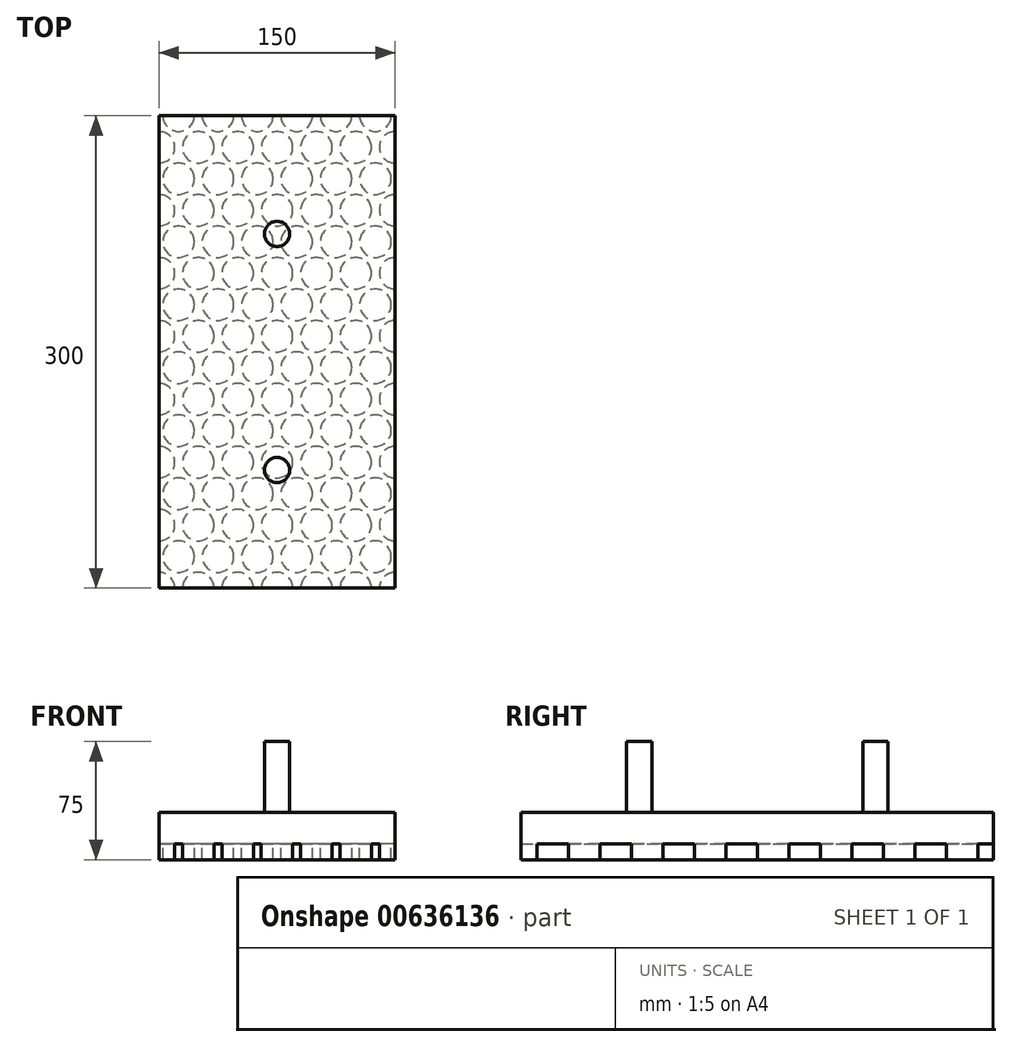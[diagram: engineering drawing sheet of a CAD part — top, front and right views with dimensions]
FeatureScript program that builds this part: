
annotation { "Feature Type Name" : "Feature", "Feature Type Description" : "" }
export const myFeature = defineFeature(function(context is Context, id is Id, definition is map)
    precondition{}
    {
        {
            var Q0;
            Q0=qCreatedBy(makeId("Top.planeOp"),FACE);
            var sketch = newSketch(context, id + "F0", { "sketchPlane" : qUnion([Q0])});
            skLineSegment(sketch, "E0.bottom", {"start": v(75, 150) * mm, "end": v(-75, 150) * mm});
            skLineSegment(sketch, "E0.top", {"start": v(75, -150) * mm, "end": v(-75, -150) * mm});
            skLineSegment(sketch, "E0.left", {"start": v(75, 150) * mm, "end": v(75, -150) * mm});
            skLineSegment(sketch, "E0.right", {"start": v(-75, 150) * mm, "end": v(-75, -150) * mm});
            skPoint(sketch, "E0.middle", {"position": v(0, 0) * mm});
            skSolve(sketch);
        }
        {
            var Q0;
            Q0=qSketchRegion(id+"F0",true);
            extrude(context, id + "F1", {"entities" : qUnion([Q0]), "oppositeDirection" : true, "depth" : 20 * mm, "offsetDistance" : 25 * mm});
        }
        {
            var Q0;
            Q0=makeQuery(id+"F1.opExtrude","CAP_FACE",FACE,{"disambiguationData":[OSD([sQuery(id+"F0.wireOp",EDGE,"E0.bottom"),sQuery(id+"F0.wireOp",EDGE,"E0.top"),sQuery(id+"F0.wireOp",EDGE,"E0.left"),sQuery(id+"F0.wireOp",EDGE,"E0.right"),sQuery(id+"F0.wireOp",EDGE,"dzeue0mq-ryTN-MEcJ-6Cr2-TIuR5wwS6aSh"),sQuery(id+"F0.wireOp",EDGE,"DPBKmNIL-XfQO-MkqB-CjDe-bxSWGcwg6vfk"),sQuery(id+"F0.wireOp",EDGE,"v2nlQ9jK-8eDu-H6yK-LcaL-di8VHofIcNa3"),sQuery(id+"F0.wireOp",EDGE,"Z1CVN7Bm-QXrQ-2ffn-gUqZ-VcZKbfZv5ewL")])],"isStart":true});
            var sketch = newSketch(context, id + "F2", { "sketchPlane" : qUnion([Q0])});
            skCircle(sketch, "E1", {"center": v(0, 75) * mm, "radius": 8 * mm});
            skCircle(sketch, "E2", {"center": v(0, -75) * mm, "radius": 8 * mm});
            skSolve(sketch);
        }
        {
            var Q0;
            Q0=qSketchRegion(id+"F2",true);
            extrude(context, id + "F3", {"entities" : qUnion([Q0]), "operationType" : NewBodyOperationType.ADD, "depth" : 45 * mm, "offsetDistance" : 25 * mm});
        }
        {
            var Q0;
            Q0=makeQuery(id+"F1.opExtrude","CAP_FACE",FACE,{"disambiguationData":[OSD([sQuery(id+"F0.wireOp",EDGE,"E0.bottom"),sQuery(id+"F0.wireOp",EDGE,"E0.top"),sQuery(id+"F0.wireOp",EDGE,"E0.left"),sQuery(id+"F0.wireOp",EDGE,"E0.right")])],"isStart":false});
            var sketch = newSketch(context, id + "F4", { "sketchPlane" : qUnion([Q0])});
            skCircle(sketch, "E3", {"center": v(-75.01, 150) * mm, "radius": 10 * mm});
            skCircle(sketch, "E4", {"center": v(-62.5, 130) * mm, "radius": 10 * mm});
            skCircle(sketch, "E5.0.1.0", {"center": v(-75, 110) * mm, "radius": 10 * mm});
            skCircle(sketch, "E5.0.2.0", {"center": v(-75, 70) * mm, "radius": 10 * mm});
            skCircle(sketch, "E5.0.3.0", {"center": v(-75, 30) * mm, "radius": 10 * mm});
            skCircle(sketch, "E5.0.4.0", {"center": v(-75, -10) * mm, "radius": 10 * mm});
            skCircle(sketch, "E5.0.5.0", {"center": v(-75, -50) * mm, "radius": 10 * mm});
            skCircle(sketch, "E5.0.6.0", {"center": v(-75, -90) * mm, "radius": 10 * mm});
            skCircle(sketch, "E5.0.7.0", {"center": v(-75, -130) * mm, "radius": 10 * mm});
            skCircle(sketch, "E5.1.0.0", {"center": v(-50.01, 150) * mm, "radius": 10 * mm});
            skCircle(sketch, "E5.1.1.0", {"center": v(-50, 110) * mm, "radius": 10 * mm});
            skCircle(sketch, "E5.1.2.0", {"center": v(-50, 70) * mm, "radius": 10 * mm});
            skCircle(sketch, "E5.1.3.0", {"center": v(-50, 30) * mm, "radius": 10 * mm});
            skCircle(sketch, "E5.1.4.0", {"center": v(-50, -10) * mm, "radius": 10 * mm});
            skCircle(sketch, "E5.1.5.0", {"center": v(-50, -50) * mm, "radius": 10 * mm});
            skCircle(sketch, "E5.1.6.0", {"center": v(-50, -90) * mm, "radius": 10 * mm});
            skCircle(sketch, "E5.1.7.0", {"center": v(-50, -130) * mm, "radius": 10 * mm});
            skCircle(sketch, "E5.2.0.0", {"center": v(-25.01, 150) * mm, "radius": 10 * mm});
            skCircle(sketch, "E5.2.1.0", {"center": v(-25.01, 110) * mm, "radius": 10 * mm});
            skCircle(sketch, "E5.2.2.0", {"center": v(-25, 70) * mm, "radius": 10 * mm});
            skCircle(sketch, "E5.2.3.0", {"center": v(-25, 30) * mm, "radius": 10 * mm});
            skCircle(sketch, "E5.2.4.0", {"center": v(-25, -10) * mm, "radius": 10 * mm});
            skCircle(sketch, "E5.2.5.0", {"center": v(-25, -50) * mm, "radius": 10 * mm});
            skCircle(sketch, "E5.2.6.0", {"center": v(-25, -90) * mm, "radius": 10 * mm});
            skCircle(sketch, "E5.2.7.0", {"center": v(-25, -130) * mm, "radius": 10 * mm});
            skCircle(sketch, "E5.3.0.0", {"center": v(-0.01, 150) * mm, "radius": 10 * mm});
            skCircle(sketch, "E5.3.1.0", {"center": v(-0.01, 110) * mm, "radius": 10 * mm});
            skCircle(sketch, "E5.3.2.0", {"center": v(0, 70) * mm, "radius": 10 * mm});
            skCircle(sketch, "E5.3.3.0", {"center": v(0, 30) * mm, "radius": 10 * mm});
            skCircle(sketch, "E5.3.4.0", {"center": v(0, -10) * mm, "radius": 10 * mm});
            skCircle(sketch, "E5.3.5.0", {"center": v(0, -50) * mm, "radius": 10 * mm});
            skCircle(sketch, "E5.3.6.0", {"center": v(0, -90) * mm, "radius": 10 * mm});
            skCircle(sketch, "E5.3.7.0", {"center": v(0, -130) * mm, "radius": 10 * mm});
            skCircle(sketch, "E5.4.0.0", {"center": v(24.99, 150) * mm, "radius": 10 * mm});
            skCircle(sketch, "E5.4.1.0", {"center": v(24.99, 110) * mm, "radius": 10 * mm});
            skCircle(sketch, "E5.4.2.0", {"center": v(24.99, 70) * mm, "radius": 10 * mm});
            skCircle(sketch, "E5.4.3.0", {"center": v(25, 30) * mm, "radius": 10 * mm});
            skCircle(sketch, "E5.4.4.0", {"center": v(25, -10) * mm, "radius": 10 * mm});
            skCircle(sketch, "E5.4.5.0", {"center": v(25, -50) * mm, "radius": 10 * mm});
            skCircle(sketch, "E5.4.6.0", {"center": v(25, -90) * mm, "radius": 10 * mm});
            skCircle(sketch, "E5.4.7.0", {"center": v(25, -130) * mm, "radius": 10 * mm});
            skCircle(sketch, "E5.5.0.0", {"center": v(49.99, 150) * mm, "radius": 10 * mm});
            skCircle(sketch, "E5.5.1.0", {"center": v(49.99, 110) * mm, "radius": 10 * mm});
            skCircle(sketch, "E5.5.2.0", {"center": v(49.99, 70) * mm, "radius": 10 * mm});
            skCircle(sketch, "E5.5.3.0", {"center": v(49.99, 30) * mm, "radius": 10 * mm});
            skCircle(sketch, "E5.5.4.0", {"center": v(50, -10) * mm, "radius": 10 * mm});
            skCircle(sketch, "E5.5.5.0", {"center": v(50, -50) * mm, "radius": 10 * mm});
            skCircle(sketch, "E5.5.6.0", {"center": v(50, -90) * mm, "radius": 10 * mm});
            skCircle(sketch, "E5.5.7.0", {"center": v(50, -130) * mm, "radius": 10 * mm});
            skCircle(sketch, "E5.6.0.0", {"center": v(74.99, 150) * mm, "radius": 10 * mm});
            skCircle(sketch, "E5.6.1.0", {"center": v(74.99, 110) * mm, "radius": 10 * mm});
            skCircle(sketch, "E5.6.2.0", {"center": v(74.99, 70) * mm, "radius": 10 * mm});
            skCircle(sketch, "E5.6.3.0", {"center": v(74.99, 30) * mm, "radius": 10 * mm});
            skCircle(sketch, "E5.6.4.0", {"center": v(75, -10) * mm, "radius": 10 * mm});
            skCircle(sketch, "E5.6.5.0", {"center": v(75, -50) * mm, "radius": 10 * mm});
            skCircle(sketch, "E5.6.6.0", {"center": v(75, -90) * mm, "radius": 10 * mm});
            skCircle(sketch, "E5.6.7.0", {"center": v(75, -130) * mm, "radius": 10 * mm});
            skLineSegment(sketch, "E5.direction1", {"start": v(-75.01, 150) * mm, "end": v(-50.01, 150) * mm, "construction": true});
            skLineSegment(sketch, "E5.direction2", {"start": v(-75.01, 150) * mm, "end": v(-75.01, 110) * mm, "construction": true});
            skCircle(sketch, "E6.0.1.0", {"center": v(-62.5, 90) * mm, "radius": 10 * mm});
            skCircle(sketch, "E6.0.2.0", {"center": v(-62.5, 50) * mm, "radius": 10 * mm});
            skCircle(sketch, "E6.0.3.0", {"center": v(-62.5, 10) * mm, "radius": 10 * mm});
            skCircle(sketch, "E6.0.4.0", {"center": v(-62.5, -30) * mm, "radius": 10 * mm});
            skCircle(sketch, "E6.0.5.0", {"center": v(-62.5, -70) * mm, "radius": 10 * mm});
            skCircle(sketch, "E6.0.6.0", {"center": v(-62.5, -110) * mm, "radius": 10 * mm});
            skCircle(sketch, "E6.0.7.0", {"center": v(-62.5, -150) * mm, "radius": 10 * mm});
            skCircle(sketch, "E6.1.0.0", {"center": v(-37.5, 130) * mm, "radius": 10 * mm});
            skCircle(sketch, "E6.1.1.0", {"center": v(-37.5, 90) * mm, "radius": 10 * mm});
            skCircle(sketch, "E6.1.2.0", {"center": v(-37.5, 50) * mm, "radius": 10 * mm});
            skCircle(sketch, "E6.1.3.0", {"center": v(-37.5, 10) * mm, "radius": 10 * mm});
            skCircle(sketch, "E6.1.4.0", {"center": v(-37.5, -30) * mm, "radius": 10 * mm});
            skCircle(sketch, "E6.1.5.0", {"center": v(-37.5, -70) * mm, "radius": 10 * mm});
            skCircle(sketch, "E6.1.6.0", {"center": v(-37.5, -110) * mm, "radius": 10 * mm});
            skCircle(sketch, "E6.1.7.0", {"center": v(-37.5, -150) * mm, "radius": 10 * mm});
            skCircle(sketch, "E6.2.0.0", {"center": v(-12.5, 130) * mm, "radius": 10 * mm});
            skCircle(sketch, "E6.2.1.0", {"center": v(-12.5, 90) * mm, "radius": 10 * mm});
            skCircle(sketch, "E6.2.2.0", {"center": v(-12.5, 50) * mm, "radius": 10 * mm});
            skCircle(sketch, "E6.2.3.0", {"center": v(-12.5, 10) * mm, "radius": 10 * mm});
            skCircle(sketch, "E6.2.4.0", {"center": v(-12.5, -30) * mm, "radius": 10 * mm});
            skCircle(sketch, "E6.2.5.0", {"center": v(-12.5, -70) * mm, "radius": 10 * mm});
            skCircle(sketch, "E6.2.6.0", {"center": v(-12.5, -110) * mm, "radius": 10 * mm});
            skCircle(sketch, "E6.2.7.0", {"center": v(-12.5, -150) * mm, "radius": 10 * mm});
            skCircle(sketch, "E6.3.0.0", {"center": v(12.5, 130) * mm, "radius": 10 * mm});
            skCircle(sketch, "E6.3.1.0", {"center": v(12.5, 90) * mm, "radius": 10 * mm});
            skCircle(sketch, "E6.3.2.0", {"center": v(12.5, 50) * mm, "radius": 10 * mm});
            skCircle(sketch, "E6.3.3.0", {"center": v(12.5, 10) * mm, "radius": 10 * mm});
            skCircle(sketch, "E6.3.4.0", {"center": v(12.5, -30) * mm, "radius": 10 * mm});
            skCircle(sketch, "E6.3.5.0", {"center": v(12.5, -70) * mm, "radius": 10 * mm});
            skCircle(sketch, "E6.3.6.0", {"center": v(12.5, -110) * mm, "radius": 10 * mm});
            skCircle(sketch, "E6.3.7.0", {"center": v(12.5, -150) * mm, "radius": 10 * mm});
            skCircle(sketch, "E6.4.0.0", {"center": v(37.5, 130) * mm, "radius": 10 * mm});
            skCircle(sketch, "E6.4.1.0", {"center": v(37.5, 90) * mm, "radius": 10 * mm});
            skCircle(sketch, "E6.4.2.0", {"center": v(37.5, 50) * mm, "radius": 10 * mm});
            skCircle(sketch, "E6.4.3.0", {"center": v(37.5, 10) * mm, "radius": 10 * mm});
            skCircle(sketch, "E6.4.4.0", {"center": v(37.5, -30) * mm, "radius": 10 * mm});
            skCircle(sketch, "E6.4.5.0", {"center": v(37.5, -70) * mm, "radius": 10 * mm});
            skCircle(sketch, "E6.4.6.0", {"center": v(37.5, -110) * mm, "radius": 10 * mm});
            skCircle(sketch, "E6.4.7.0", {"center": v(37.5, -150) * mm, "radius": 10 * mm});
            skCircle(sketch, "E6.5.0.0", {"center": v(62.5, 130) * mm, "radius": 10 * mm});
            skCircle(sketch, "E6.5.1.0", {"center": v(62.5, 90) * mm, "radius": 10 * mm});
            skCircle(sketch, "E6.5.2.0", {"center": v(62.5, 50) * mm, "radius": 10 * mm});
            skCircle(sketch, "E6.5.3.0", {"center": v(62.5, 10) * mm, "radius": 10 * mm});
            skCircle(sketch, "E6.5.4.0", {"center": v(62.5, -30) * mm, "radius": 10 * mm});
            skCircle(sketch, "E6.5.5.0", {"center": v(62.5, -70) * mm, "radius": 10 * mm});
            skCircle(sketch, "E6.5.6.0", {"center": v(62.5, -110) * mm, "radius": 10 * mm});
            skCircle(sketch, "E6.5.7.0", {"center": v(62.5, -150) * mm, "radius": 10 * mm});
            skLineSegment(sketch, "E6.direction1", {"start": v(-62.5, 130) * mm, "end": v(-37.5, 130) * mm, "construction": true});
            skLineSegment(sketch, "E6.direction2", {"start": v(-62.5, 130) * mm, "end": v(-62.5, 90) * mm, "construction": true});
            skSolve(sketch);
        }
        {
            var Q0;
            Q0=makeQuery(id+"F4.imprint","IMPRINT",FACE,{"disambiguationData":[TD([[makeQuery(id+"F4.imprint","IMPRINT",EDGE,{"derivedFrom":sQuery(id+"F4.wireOp",EDGE,"E4")}),1.0]])]});
            var Q1;
            Q1=makeQuery(id+"F4.imprint","IMPRINT",FACE,{"disambiguationData":[TD([[makeQuery(id+"F4.imprint","IMPRINT",EDGE,{"derivedFrom":sQuery(id+"F4.wireOp",EDGE,"E5.1.1.0")}),1.0]])]});
            var Q2;
            Q2=makeQuery(id+"F4.imprint","IMPRINT",FACE,{"disambiguationData":[TD([[makeQuery(id+"F4.imprint","IMPRINT",EDGE,{"derivedFrom":sQuery(id+"F4.wireOp",EDGE,"E5.1.2.0")}),1.0]])]});
            var Q3;
            Q3=makeQuery(id+"F4.imprint","IMPRINT",FACE,{"disambiguationData":[TD([[makeQuery(id+"F4.imprint","IMPRINT",EDGE,{"derivedFrom":sQuery(id+"F4.wireOp",EDGE,"E5.1.3.0")}),1.0]])]});
            var Q4;
            Q4=makeQuery(id+"F4.imprint","IMPRINT",FACE,{"disambiguationData":[TD([[makeQuery(id+"F4.imprint","IMPRINT",EDGE,{"derivedFrom":sQuery(id+"F4.wireOp",EDGE,"E5.1.4.0")}),1.0]])]});
            var Q5;
            Q5=makeQuery(id+"F4.imprint","IMPRINT",FACE,{"disambiguationData":[TD([[makeQuery(id+"F4.imprint","IMPRINT",EDGE,{"derivedFrom":sQuery(id+"F4.wireOp",EDGE,"E5.1.5.0")}),1.0]])]});
            var Q6;
            Q6=makeQuery(id+"F4.imprint","IMPRINT",FACE,{"disambiguationData":[TD([[makeQuery(id+"F4.imprint","IMPRINT",EDGE,{"derivedFrom":sQuery(id+"F4.wireOp",EDGE,"E5.1.6.0")}),1.0]])]});
            var Q7;
            Q7=makeQuery(id+"F4.imprint","IMPRINT",FACE,{"disambiguationData":[TD([[makeQuery(id+"F4.imprint","IMPRINT",EDGE,{"derivedFrom":sQuery(id+"F4.wireOp",EDGE,"E5.1.7.0")}),1.0]])]});
            var Q8;
            Q8=makeQuery(id+"F4.imprint","IMPRINT",FACE,{"disambiguationData":[TD([[makeQuery(id+"F4.imprint","IMPRINT",EDGE,{"derivedFrom":sQuery(id+"F4.wireOp",EDGE,"E5.2.1.0")}),1.0]])]});
            var Q9;
            Q9=makeQuery(id+"F4.imprint","IMPRINT",FACE,{"disambiguationData":[TD([[makeQuery(id+"F4.imprint","IMPRINT",EDGE,{"derivedFrom":sQuery(id+"F4.wireOp",EDGE,"E5.2.2.0")}),1.0]])]});
            var Q10;
            Q10=makeQuery(id+"F4.imprint","IMPRINT",FACE,{"disambiguationData":[TD([[makeQuery(id+"F4.imprint","IMPRINT",EDGE,{"derivedFrom":sQuery(id+"F4.wireOp",EDGE,"E5.2.3.0")}),1.0]])]});
            var Q11;
            Q11=makeQuery(id+"F4.imprint","IMPRINT",FACE,{"disambiguationData":[TD([[makeQuery(id+"F4.imprint","IMPRINT",EDGE,{"derivedFrom":sQuery(id+"F4.wireOp",EDGE,"E5.2.4.0")}),1.0]])]});
            var Q12;
            Q12=makeQuery(id+"F4.imprint","IMPRINT",FACE,{"disambiguationData":[TD([[makeQuery(id+"F4.imprint","IMPRINT",EDGE,{"derivedFrom":sQuery(id+"F4.wireOp",EDGE,"E5.2.5.0")}),1.0]])]});
            var Q13;
            Q13=makeQuery(id+"F4.imprint","IMPRINT",FACE,{"disambiguationData":[TD([[makeQuery(id+"F4.imprint","IMPRINT",EDGE,{"derivedFrom":sQuery(id+"F4.wireOp",EDGE,"E5.2.6.0")}),1.0]])]});
            var Q14;
            Q14=makeQuery(id+"F4.imprint","IMPRINT",FACE,{"disambiguationData":[TD([[makeQuery(id+"F4.imprint","IMPRINT",EDGE,{"derivedFrom":sQuery(id+"F4.wireOp",EDGE,"E5.2.7.0")}),1.0]])]});
            var Q15;
            Q15=makeQuery(id+"F4.imprint","IMPRINT",FACE,{"disambiguationData":[TD([[makeQuery(id+"F4.imprint","IMPRINT",EDGE,{"derivedFrom":sQuery(id+"F4.wireOp",EDGE,"E5.3.1.0")}),1.0]])]});
            var Q16;
            Q16=makeQuery(id+"F4.imprint","IMPRINT",FACE,{"disambiguationData":[TD([[makeQuery(id+"F4.imprint","IMPRINT",EDGE,{"derivedFrom":sQuery(id+"F4.wireOp",EDGE,"E5.3.2.0")}),1.0]])]});
            var Q17;
            Q17=makeQuery(id+"F4.imprint","IMPRINT",FACE,{"disambiguationData":[TD([[makeQuery(id+"F4.imprint","IMPRINT",EDGE,{"derivedFrom":sQuery(id+"F4.wireOp",EDGE,"E5.3.3.0")}),1.0]])]});
            var Q18;
            Q18=makeQuery(id+"F4.imprint","IMPRINT",FACE,{"disambiguationData":[TD([[makeQuery(id+"F4.imprint","IMPRINT",EDGE,{"derivedFrom":sQuery(id+"F4.wireOp",EDGE,"E5.3.4.0")}),1.0]])]});
            var Q19;
            Q19=makeQuery(id+"F4.imprint","IMPRINT",FACE,{"disambiguationData":[TD([[makeQuery(id+"F4.imprint","IMPRINT",EDGE,{"derivedFrom":sQuery(id+"F4.wireOp",EDGE,"E5.3.5.0")}),1.0]])]});
            var Q20;
            Q20=makeQuery(id+"F4.imprint","IMPRINT",FACE,{"disambiguationData":[TD([[makeQuery(id+"F4.imprint","IMPRINT",EDGE,{"derivedFrom":sQuery(id+"F4.wireOp",EDGE,"E5.3.6.0")}),1.0]])]});
            var Q21;
            Q21=makeQuery(id+"F4.imprint","IMPRINT",FACE,{"disambiguationData":[TD([[makeQuery(id+"F4.imprint","IMPRINT",EDGE,{"derivedFrom":sQuery(id+"F4.wireOp",EDGE,"E5.3.7.0")}),1.0]])]});
            var Q22;
            Q22=makeQuery(id+"F4.imprint","IMPRINT",FACE,{"disambiguationData":[TD([[makeQuery(id+"F4.imprint","IMPRINT",EDGE,{"derivedFrom":sQuery(id+"F4.wireOp",EDGE,"E5.4.1.0")}),1.0]])]});
            var Q23;
            Q23=makeQuery(id+"F4.imprint","IMPRINT",FACE,{"disambiguationData":[TD([[makeQuery(id+"F4.imprint","IMPRINT",EDGE,{"derivedFrom":sQuery(id+"F4.wireOp",EDGE,"E5.4.2.0")}),1.0]])]});
            var Q24;
            Q24=makeQuery(id+"F4.imprint","IMPRINT",FACE,{"disambiguationData":[TD([[makeQuery(id+"F4.imprint","IMPRINT",EDGE,{"derivedFrom":sQuery(id+"F4.wireOp",EDGE,"E5.4.3.0")}),1.0]])]});
            var Q25;
            Q25=makeQuery(id+"F4.imprint","IMPRINT",FACE,{"disambiguationData":[TD([[makeQuery(id+"F4.imprint","IMPRINT",EDGE,{"derivedFrom":sQuery(id+"F4.wireOp",EDGE,"E5.4.4.0")}),1.0]])]});
            var Q26;
            Q26=makeQuery(id+"F4.imprint","IMPRINT",FACE,{"disambiguationData":[TD([[makeQuery(id+"F4.imprint","IMPRINT",EDGE,{"derivedFrom":sQuery(id+"F4.wireOp",EDGE,"E5.4.5.0")}),1.0]])]});
            var Q27;
            Q27=makeQuery(id+"F4.imprint","IMPRINT",FACE,{"disambiguationData":[TD([[makeQuery(id+"F4.imprint","IMPRINT",EDGE,{"derivedFrom":sQuery(id+"F4.wireOp",EDGE,"E5.4.6.0")}),1.0]])]});
            var Q28;
            Q28=makeQuery(id+"F4.imprint","IMPRINT",FACE,{"disambiguationData":[TD([[makeQuery(id+"F4.imprint","IMPRINT",EDGE,{"derivedFrom":sQuery(id+"F4.wireOp",EDGE,"E5.4.7.0")}),1.0]])]});
            var Q29;
            Q29=makeQuery(id+"F4.imprint","IMPRINT",FACE,{"disambiguationData":[TD([[makeQuery(id+"F4.imprint","IMPRINT",EDGE,{"derivedFrom":sQuery(id+"F4.wireOp",EDGE,"E5.5.1.0")}),1.0]])]});
            var Q30;
            Q30=makeQuery(id+"F4.imprint","IMPRINT",FACE,{"disambiguationData":[TD([[makeQuery(id+"F4.imprint","IMPRINT",EDGE,{"derivedFrom":sQuery(id+"F4.wireOp",EDGE,"E5.5.2.0")}),1.0]])]});
            var Q31;
            Q31=makeQuery(id+"F4.imprint","IMPRINT",FACE,{"disambiguationData":[TD([[makeQuery(id+"F4.imprint","IMPRINT",EDGE,{"derivedFrom":sQuery(id+"F4.wireOp",EDGE,"E5.5.3.0")}),1.0]])]});
            var Q32;
            Q32=makeQuery(id+"F4.imprint","IMPRINT",FACE,{"disambiguationData":[TD([[makeQuery(id+"F4.imprint","IMPRINT",EDGE,{"derivedFrom":sQuery(id+"F4.wireOp",EDGE,"E5.5.4.0")}),1.0]])]});
            var Q33;
            Q33=makeQuery(id+"F4.imprint","IMPRINT",FACE,{"disambiguationData":[TD([[makeQuery(id+"F4.imprint","IMPRINT",EDGE,{"derivedFrom":sQuery(id+"F4.wireOp",EDGE,"E5.5.5.0")}),1.0]])]});
            var Q34;
            Q34=makeQuery(id+"F4.imprint","IMPRINT",FACE,{"disambiguationData":[TD([[makeQuery(id+"F4.imprint","IMPRINT",EDGE,{"derivedFrom":sQuery(id+"F4.wireOp",EDGE,"E5.5.6.0")}),1.0]])]});
            var Q35;
            Q35=makeQuery(id+"F4.imprint","IMPRINT",FACE,{"disambiguationData":[TD([[makeQuery(id+"F4.imprint","IMPRINT",EDGE,{"derivedFrom":sQuery(id+"F4.wireOp",EDGE,"E5.5.7.0")}),1.0]])]});
            var Q36;
            Q36=makeQuery(id+"F4.imprint","IMPRINT",FACE,{"disambiguationData":[TD([[makeQuery(id+"F4.imprint","IMPRINT",EDGE,{"derivedFrom":sQuery(id+"F4.wireOp",EDGE,"E6.0.1.0")}),1.0]])]});
            var Q37;
            Q37=makeQuery(id+"F4.imprint","IMPRINT",FACE,{"disambiguationData":[TD([[makeQuery(id+"F4.imprint","IMPRINT",EDGE,{"derivedFrom":sQuery(id+"F4.wireOp",EDGE,"E6.0.2.0")}),1.0]])]});
            var Q38;
            Q38=makeQuery(id+"F4.imprint","IMPRINT",FACE,{"disambiguationData":[TD([[makeQuery(id+"F4.imprint","IMPRINT",EDGE,{"derivedFrom":sQuery(id+"F4.wireOp",EDGE,"E6.0.3.0")}),1.0]])]});
            var Q39;
            Q39=makeQuery(id+"F4.imprint","IMPRINT",FACE,{"disambiguationData":[TD([[makeQuery(id+"F4.imprint","IMPRINT",EDGE,{"derivedFrom":sQuery(id+"F4.wireOp",EDGE,"E6.0.4.0")}),1.0]])]});
            var Q40;
            Q40=makeQuery(id+"F4.imprint","IMPRINT",FACE,{"disambiguationData":[TD([[makeQuery(id+"F4.imprint","IMPRINT",EDGE,{"derivedFrom":sQuery(id+"F4.wireOp",EDGE,"E6.0.5.0")}),1.0]])]});
            var Q41;
            Q41=makeQuery(id+"F4.imprint","IMPRINT",FACE,{"disambiguationData":[TD([[makeQuery(id+"F4.imprint","IMPRINT",EDGE,{"derivedFrom":sQuery(id+"F4.wireOp",EDGE,"E6.0.6.0")}),1.0]])]});
            var Q42;
            Q42=makeQuery(id+"F4.imprint","IMPRINT",FACE,{"disambiguationData":[TD([[makeQuery(id+"F4.imprint","IMPRINT",EDGE,{"derivedFrom":sQuery(id+"F4.wireOp",EDGE,"E6.1.0.0")}),1.0]])]});
            var Q43;
            Q43=makeQuery(id+"F4.imprint","IMPRINT",FACE,{"disambiguationData":[TD([[makeQuery(id+"F4.imprint","IMPRINT",EDGE,{"derivedFrom":sQuery(id+"F4.wireOp",EDGE,"E6.1.1.0")}),1.0]])]});
            var Q44;
            Q44=makeQuery(id+"F4.imprint","IMPRINT",FACE,{"disambiguationData":[TD([[makeQuery(id+"F4.imprint","IMPRINT",EDGE,{"derivedFrom":sQuery(id+"F4.wireOp",EDGE,"E6.1.2.0")}),1.0]])]});
            var Q45;
            Q45=makeQuery(id+"F4.imprint","IMPRINT",FACE,{"disambiguationData":[TD([[makeQuery(id+"F4.imprint","IMPRINT",EDGE,{"derivedFrom":sQuery(id+"F4.wireOp",EDGE,"E6.1.3.0")}),1.0]])]});
            var Q46;
            Q46=makeQuery(id+"F4.imprint","IMPRINT",FACE,{"disambiguationData":[TD([[makeQuery(id+"F4.imprint","IMPRINT",EDGE,{"derivedFrom":sQuery(id+"F4.wireOp",EDGE,"E6.1.4.0")}),1.0]])]});
            var Q47;
            Q47=makeQuery(id+"F4.imprint","IMPRINT",FACE,{"disambiguationData":[TD([[makeQuery(id+"F4.imprint","IMPRINT",EDGE,{"derivedFrom":sQuery(id+"F4.wireOp",EDGE,"E6.1.5.0")}),1.0]])]});
            var Q48;
            Q48=makeQuery(id+"F4.imprint","IMPRINT",FACE,{"disambiguationData":[TD([[makeQuery(id+"F4.imprint","IMPRINT",EDGE,{"derivedFrom":sQuery(id+"F4.wireOp",EDGE,"E6.1.6.0")}),1.0]])]});
            var Q49;
            Q49=makeQuery(id+"F4.imprint","IMPRINT",FACE,{"disambiguationData":[TD([[makeQuery(id+"F4.imprint","IMPRINT",EDGE,{"derivedFrom":sQuery(id+"F4.wireOp",EDGE,"E6.2.0.0")}),1.0]])]});
            var Q50;
            Q50=makeQuery(id+"F4.imprint","IMPRINT",FACE,{"disambiguationData":[TD([[makeQuery(id+"F4.imprint","IMPRINT",EDGE,{"derivedFrom":sQuery(id+"F4.wireOp",EDGE,"E6.2.1.0")}),1.0]])]});
            var Q51;
            Q51=makeQuery(id+"F4.imprint","IMPRINT",FACE,{"disambiguationData":[TD([[makeQuery(id+"F4.imprint","IMPRINT",EDGE,{"derivedFrom":sQuery(id+"F4.wireOp",EDGE,"E6.2.2.0")}),1.0]])]});
            var Q52;
            Q52=makeQuery(id+"F4.imprint","IMPRINT",FACE,{"disambiguationData":[TD([[makeQuery(id+"F4.imprint","IMPRINT",EDGE,{"derivedFrom":sQuery(id+"F4.wireOp",EDGE,"E6.2.3.0")}),1.0]])]});
            var Q53;
            Q53=makeQuery(id+"F4.imprint","IMPRINT",FACE,{"disambiguationData":[TD([[makeQuery(id+"F4.imprint","IMPRINT",EDGE,{"derivedFrom":sQuery(id+"F4.wireOp",EDGE,"E6.2.4.0")}),1.0]])]});
            var Q54;
            Q54=makeQuery(id+"F4.imprint","IMPRINT",FACE,{"disambiguationData":[TD([[makeQuery(id+"F4.imprint","IMPRINT",EDGE,{"derivedFrom":sQuery(id+"F4.wireOp",EDGE,"E6.2.5.0")}),1.0]])]});
            var Q55;
            Q55=makeQuery(id+"F4.imprint","IMPRINT",FACE,{"disambiguationData":[TD([[makeQuery(id+"F4.imprint","IMPRINT",EDGE,{"derivedFrom":sQuery(id+"F4.wireOp",EDGE,"E6.2.6.0")}),1.0]])]});
            var Q56;
            Q56=makeQuery(id+"F4.imprint","IMPRINT",FACE,{"disambiguationData":[TD([[makeQuery(id+"F4.imprint","IMPRINT",EDGE,{"derivedFrom":sQuery(id+"F4.wireOp",EDGE,"E6.3.0.0")}),1.0]])]});
            var Q57;
            Q57=makeQuery(id+"F4.imprint","IMPRINT",FACE,{"disambiguationData":[TD([[makeQuery(id+"F4.imprint","IMPRINT",EDGE,{"derivedFrom":sQuery(id+"F4.wireOp",EDGE,"E6.3.1.0")}),1.0]])]});
            var Q58;
            Q58=makeQuery(id+"F4.imprint","IMPRINT",FACE,{"disambiguationData":[TD([[makeQuery(id+"F4.imprint","IMPRINT",EDGE,{"derivedFrom":sQuery(id+"F4.wireOp",EDGE,"E6.3.2.0")}),1.0]])]});
            var Q59;
            Q59=makeQuery(id+"F4.imprint","IMPRINT",FACE,{"disambiguationData":[TD([[makeQuery(id+"F4.imprint","IMPRINT",EDGE,{"derivedFrom":sQuery(id+"F4.wireOp",EDGE,"E6.3.3.0")}),1.0]])]});
            var Q60;
            Q60=makeQuery(id+"F4.imprint","IMPRINT",FACE,{"disambiguationData":[TD([[makeQuery(id+"F4.imprint","IMPRINT",EDGE,{"derivedFrom":sQuery(id+"F4.wireOp",EDGE,"E6.3.4.0")}),1.0]])]});
            var Q61;
            Q61=makeQuery(id+"F4.imprint","IMPRINT",FACE,{"disambiguationData":[TD([[makeQuery(id+"F4.imprint","IMPRINT",EDGE,{"derivedFrom":sQuery(id+"F4.wireOp",EDGE,"E6.3.5.0")}),1.0]])]});
            var Q62;
            Q62=makeQuery(id+"F4.imprint","IMPRINT",FACE,{"disambiguationData":[TD([[makeQuery(id+"F4.imprint","IMPRINT",EDGE,{"derivedFrom":sQuery(id+"F4.wireOp",EDGE,"E6.3.6.0")}),1.0]])]});
            var Q63;
            Q63=makeQuery(id+"F4.imprint","IMPRINT",FACE,{"disambiguationData":[TD([[makeQuery(id+"F4.imprint","IMPRINT",EDGE,{"derivedFrom":sQuery(id+"F4.wireOp",EDGE,"E6.4.0.0")}),1.0]])]});
            var Q64;
            Q64=makeQuery(id+"F4.imprint","IMPRINT",FACE,{"disambiguationData":[TD([[makeQuery(id+"F4.imprint","IMPRINT",EDGE,{"derivedFrom":sQuery(id+"F4.wireOp",EDGE,"E6.4.1.0")}),1.0]])]});
            var Q65;
            Q65=makeQuery(id+"F4.imprint","IMPRINT",FACE,{"disambiguationData":[TD([[makeQuery(id+"F4.imprint","IMPRINT",EDGE,{"derivedFrom":sQuery(id+"F4.wireOp",EDGE,"E6.4.2.0")}),1.0]])]});
            var Q66;
            Q66=makeQuery(id+"F4.imprint","IMPRINT",FACE,{"disambiguationData":[TD([[makeQuery(id+"F4.imprint","IMPRINT",EDGE,{"derivedFrom":sQuery(id+"F4.wireOp",EDGE,"E6.4.3.0")}),1.0]])]});
            var Q67;
            Q67=makeQuery(id+"F4.imprint","IMPRINT",FACE,{"disambiguationData":[TD([[makeQuery(id+"F4.imprint","IMPRINT",EDGE,{"derivedFrom":sQuery(id+"F4.wireOp",EDGE,"E6.4.4.0")}),1.0]])]});
            var Q68;
            Q68=makeQuery(id+"F4.imprint","IMPRINT",FACE,{"disambiguationData":[TD([[makeQuery(id+"F4.imprint","IMPRINT",EDGE,{"derivedFrom":sQuery(id+"F4.wireOp",EDGE,"E6.4.5.0")}),1.0]])]});
            var Q69;
            Q69=makeQuery(id+"F4.imprint","IMPRINT",FACE,{"disambiguationData":[TD([[makeQuery(id+"F4.imprint","IMPRINT",EDGE,{"derivedFrom":sQuery(id+"F4.wireOp",EDGE,"E6.4.6.0")}),1.0]])]});
            var Q70;
            Q70=makeQuery(id+"F4.imprint","IMPRINT",FACE,{"disambiguationData":[TD([[makeQuery(id+"F4.imprint","IMPRINT",EDGE,{"derivedFrom":sQuery(id+"F4.wireOp",EDGE,"E6.5.0.0")}),1.0]])]});
            var Q71;
            Q71=makeQuery(id+"F4.imprint","IMPRINT",FACE,{"disambiguationData":[TD([[makeQuery(id+"F4.imprint","IMPRINT",EDGE,{"derivedFrom":sQuery(id+"F4.wireOp",EDGE,"E6.5.1.0")}),1.0]])]});
            var Q72;
            Q72=makeQuery(id+"F4.imprint","IMPRINT",FACE,{"disambiguationData":[TD([[makeQuery(id+"F4.imprint","IMPRINT",EDGE,{"derivedFrom":sQuery(id+"F4.wireOp",EDGE,"E6.5.2.0")}),1.0]])]});
            var Q73;
            Q73=makeQuery(id+"F4.imprint","IMPRINT",FACE,{"disambiguationData":[TD([[makeQuery(id+"F4.imprint","IMPRINT",EDGE,{"derivedFrom":sQuery(id+"F4.wireOp",EDGE,"E6.5.3.0")}),1.0]])]});
            var Q74;
            Q74=makeQuery(id+"F4.imprint","IMPRINT",FACE,{"disambiguationData":[TD([[makeQuery(id+"F4.imprint","IMPRINT",EDGE,{"derivedFrom":sQuery(id+"F4.wireOp",EDGE,"E6.5.4.0")}),1.0]])]});
            var Q75;
            Q75=makeQuery(id+"F4.imprint","IMPRINT",FACE,{"disambiguationData":[TD([[makeQuery(id+"F4.imprint","IMPRINT",EDGE,{"derivedFrom":sQuery(id+"F4.wireOp",EDGE,"E6.5.5.0")}),1.0]])]});
            var Q76;
            Q76=makeQuery(id+"F4.imprint","IMPRINT",FACE,{"disambiguationData":[TD([[makeQuery(id+"F4.imprint","IMPRINT",EDGE,{"derivedFrom":sQuery(id+"F4.wireOp",EDGE,"E6.5.6.0")}),1.0]])]});
            var Q77;
            {var subQ0=sQuery(id+"F4.wireOp",EDGE,"E5.0.1.0");var subQ1=makeQuery(id+"F1.opExtrude","CAP_EDGE",EDGE,{"disambiguationData":[OSD([sQuery(id+"F0.wireOp",EDGE,"E0.right")])],"isStart":false});var subQ2=makeQuery(id+"F4.imprint","INTERSECT",VERTEX,{"disambiguationData":[OD(0.0)],"derivedFrom":[subQ1,subQ0]});Q77=makeQuery(id+"F4.imprint","IMPRINT",FACE,{"disambiguationData":[TD([[makeQuery(id+"F4.imprint","IMPRINT",EDGE,{"disambiguationData":[TD([[subQ2,1.0]])],"derivedFrom":subQ0}),1.0]])]});}
            var Q78;
            {var subQ0=sQuery(id+"F4.wireOp",EDGE,"E5.0.2.0");var subQ1=makeQuery(id+"F1.opExtrude","CAP_EDGE",EDGE,{"disambiguationData":[OSD([sQuery(id+"F0.wireOp",EDGE,"E0.right")])],"isStart":false});var subQ2=makeQuery(id+"F4.imprint","INTERSECT",VERTEX,{"disambiguationData":[OD(0.0)],"derivedFrom":[subQ1,subQ0]});Q78=makeQuery(id+"F4.imprint","IMPRINT",FACE,{"disambiguationData":[TD([[makeQuery(id+"F4.imprint","IMPRINT",EDGE,{"disambiguationData":[TD([[subQ2,1.0]])],"derivedFrom":subQ0}),1.0]])]});}
            var Q79;
            {var subQ0=sQuery(id+"F4.wireOp",EDGE,"E5.0.3.0");var subQ1=makeQuery(id+"F1.opExtrude","CAP_EDGE",EDGE,{"disambiguationData":[OSD([sQuery(id+"F0.wireOp",EDGE,"E0.right")])],"isStart":false});var subQ2=makeQuery(id+"F4.imprint","INTERSECT",VERTEX,{"disambiguationData":[OD(0.0)],"derivedFrom":[subQ1,subQ0]});Q79=makeQuery(id+"F4.imprint","IMPRINT",FACE,{"disambiguationData":[TD([[makeQuery(id+"F4.imprint","IMPRINT",EDGE,{"disambiguationData":[TD([[subQ2,1.0]])],"derivedFrom":subQ0}),1.0]])]});}
            var Q80;
            {var subQ0=sQuery(id+"F4.wireOp",EDGE,"E5.0.4.0");var subQ1=makeQuery(id+"F1.opExtrude","CAP_EDGE",EDGE,{"disambiguationData":[OSD([sQuery(id+"F0.wireOp",EDGE,"E0.right")])],"isStart":false});var subQ2=makeQuery(id+"F4.imprint","INTERSECT",VERTEX,{"disambiguationData":[OD(0.0)],"derivedFrom":[subQ1,subQ0]});Q80=makeQuery(id+"F4.imprint","IMPRINT",FACE,{"disambiguationData":[TD([[makeQuery(id+"F4.imprint","IMPRINT",EDGE,{"disambiguationData":[TD([[subQ2,-1.0]])],"derivedFrom":subQ0}),1.0]])]});}
            var Q81;
            {var subQ0=sQuery(id+"F4.wireOp",EDGE,"E5.0.5.0");var subQ1=makeQuery(id+"F1.opExtrude","CAP_EDGE",EDGE,{"disambiguationData":[OSD([sQuery(id+"F0.wireOp",EDGE,"E0.right")])],"isStart":false});var subQ2=makeQuery(id+"F4.imprint","INTERSECT",VERTEX,{"disambiguationData":[OD(0.0)],"derivedFrom":[subQ1,subQ0]});Q81=makeQuery(id+"F4.imprint","IMPRINT",FACE,{"disambiguationData":[TD([[makeQuery(id+"F4.imprint","IMPRINT",EDGE,{"disambiguationData":[TD([[subQ2,-1.0]])],"derivedFrom":subQ0}),1.0]])]});}
            var Q82;
            {var subQ0=sQuery(id+"F4.wireOp",EDGE,"E5.0.6.0");var subQ1=makeQuery(id+"F1.opExtrude","CAP_EDGE",EDGE,{"disambiguationData":[OSD([sQuery(id+"F0.wireOp",EDGE,"E0.right")])],"isStart":false});var subQ2=makeQuery(id+"F4.imprint","INTERSECT",VERTEX,{"disambiguationData":[OD(0.0)],"derivedFrom":[subQ1,subQ0]});Q82=makeQuery(id+"F4.imprint","IMPRINT",FACE,{"disambiguationData":[TD([[makeQuery(id+"F4.imprint","IMPRINT",EDGE,{"disambiguationData":[TD([[subQ2,-1.0]])],"derivedFrom":subQ0}),1.0]])]});}
            var Q83;
            {var subQ0=sQuery(id+"F4.wireOp",EDGE,"E5.0.7.0");var subQ1=makeQuery(id+"F1.opExtrude","CAP_EDGE",EDGE,{"disambiguationData":[OSD([sQuery(id+"F0.wireOp",EDGE,"E0.right")])],"isStart":false});var subQ2=makeQuery(id+"F4.imprint","INTERSECT",VERTEX,{"disambiguationData":[OD(0.0)],"derivedFrom":[subQ1,subQ0]});Q83=makeQuery(id+"F4.imprint","IMPRINT",FACE,{"disambiguationData":[TD([[makeQuery(id+"F4.imprint","IMPRINT",EDGE,{"disambiguationData":[TD([[subQ2,-1.0]])],"derivedFrom":subQ0}),1.0]])]});}
            var Q84;
            {var subQ0=sQuery(id+"F4.wireOp",EDGE,"E5.1.0.0");var subQ1=makeQuery(id+"F1.opExtrude","CAP_EDGE",EDGE,{"disambiguationData":[OSD([sQuery(id+"F0.wireOp",EDGE,"E0.top")])],"isStart":false});var subQ2=makeQuery(id+"F4.imprint","INTERSECT",VERTEX,{"disambiguationData":[OD(0.0)],"derivedFrom":[subQ1,subQ0]});Q84=makeQuery(id+"F4.imprint","IMPRINT",FACE,{"disambiguationData":[TD([[makeQuery(id+"F4.imprint","IMPRINT",EDGE,{"disambiguationData":[TD([[subQ2,-1.0]])],"derivedFrom":subQ0}),1.0]])]});}
            var Q85;
            {var subQ0=sQuery(id+"F4.wireOp",EDGE,"E5.2.0.0");var subQ1=makeQuery(id+"F1.opExtrude","CAP_EDGE",EDGE,{"disambiguationData":[OSD([sQuery(id+"F0.wireOp",EDGE,"E0.top")])],"isStart":false});var subQ2=makeQuery(id+"F4.imprint","INTERSECT",VERTEX,{"disambiguationData":[OD(0.0)],"derivedFrom":[subQ1,subQ0]});Q85=makeQuery(id+"F4.imprint","IMPRINT",FACE,{"disambiguationData":[TD([[makeQuery(id+"F4.imprint","IMPRINT",EDGE,{"disambiguationData":[TD([[subQ2,-1.0]])],"derivedFrom":subQ0}),1.0]])]});}
            var Q86;
            {var subQ0=sQuery(id+"F4.wireOp",EDGE,"E5.3.0.0");var subQ1=makeQuery(id+"F1.opExtrude","CAP_EDGE",EDGE,{"disambiguationData":[OSD([sQuery(id+"F0.wireOp",EDGE,"E0.top")])],"isStart":false});var subQ2=makeQuery(id+"F4.imprint","INTERSECT",VERTEX,{"disambiguationData":[OD(0.0)],"derivedFrom":[subQ1,subQ0]});Q86=makeQuery(id+"F4.imprint","IMPRINT",FACE,{"disambiguationData":[TD([[makeQuery(id+"F4.imprint","IMPRINT",EDGE,{"disambiguationData":[TD([[subQ2,-1.0]])],"derivedFrom":subQ0}),1.0]])]});}
            var Q87;
            {var subQ0=sQuery(id+"F4.wireOp",EDGE,"E5.4.0.0");var subQ1=makeQuery(id+"F1.opExtrude","CAP_EDGE",EDGE,{"disambiguationData":[OSD([sQuery(id+"F0.wireOp",EDGE,"E0.top")])],"isStart":false});var subQ2=makeQuery(id+"F4.imprint","INTERSECT",VERTEX,{"disambiguationData":[OD(0.0)],"derivedFrom":[subQ1,subQ0]});Q87=makeQuery(id+"F4.imprint","IMPRINT",FACE,{"disambiguationData":[TD([[makeQuery(id+"F4.imprint","IMPRINT",EDGE,{"disambiguationData":[TD([[subQ2,1.0]])],"derivedFrom":subQ0}),1.0]])]});}
            var Q88;
            {var subQ0=sQuery(id+"F4.wireOp",EDGE,"E5.5.0.0");var subQ1=makeQuery(id+"F1.opExtrude","CAP_EDGE",EDGE,{"disambiguationData":[OSD([sQuery(id+"F0.wireOp",EDGE,"E0.top")])],"isStart":false});var subQ2=makeQuery(id+"F4.imprint","INTERSECT",VERTEX,{"disambiguationData":[OD(0.0)],"derivedFrom":[subQ1,subQ0]});Q88=makeQuery(id+"F4.imprint","IMPRINT",FACE,{"disambiguationData":[TD([[makeQuery(id+"F4.imprint","IMPRINT",EDGE,{"disambiguationData":[TD([[subQ2,1.0]])],"derivedFrom":subQ0}),1.0]])]});}
            var Q89;
            {var subQ0=sQuery(id+"F4.wireOp",EDGE,"E5.6.1.0");var subQ1=makeQuery(id+"F1.opExtrude","CAP_EDGE",EDGE,{"disambiguationData":[OSD([sQuery(id+"F0.wireOp",EDGE,"E0.left")])],"isStart":false});var subQ2=makeQuery(id+"F4.imprint","INTERSECT",VERTEX,{"disambiguationData":[OD(0.0)],"derivedFrom":[subQ1,subQ0]});Q89=makeQuery(id+"F4.imprint","IMPRINT",FACE,{"disambiguationData":[TD([[makeQuery(id+"F4.imprint","IMPRINT",EDGE,{"disambiguationData":[TD([[subQ2,-1.0]])],"derivedFrom":subQ0}),1.0]])]});}
            var Q90;
            {var subQ0=sQuery(id+"F4.wireOp",EDGE,"E5.6.2.0");var subQ1=makeQuery(id+"F1.opExtrude","CAP_EDGE",EDGE,{"disambiguationData":[OSD([sQuery(id+"F0.wireOp",EDGE,"E0.left")])],"isStart":false});var subQ2=makeQuery(id+"F4.imprint","INTERSECT",VERTEX,{"disambiguationData":[OD(0.0)],"derivedFrom":[subQ1,subQ0]});Q90=makeQuery(id+"F4.imprint","IMPRINT",FACE,{"disambiguationData":[TD([[makeQuery(id+"F4.imprint","IMPRINT",EDGE,{"disambiguationData":[TD([[subQ2,-1.0]])],"derivedFrom":subQ0}),1.0]])]});}
            var Q91;
            {var subQ0=sQuery(id+"F4.wireOp",EDGE,"E5.6.3.0");var subQ1=makeQuery(id+"F1.opExtrude","CAP_EDGE",EDGE,{"disambiguationData":[OSD([sQuery(id+"F0.wireOp",EDGE,"E0.left")])],"isStart":false});var subQ2=makeQuery(id+"F4.imprint","INTERSECT",VERTEX,{"disambiguationData":[OD(0.0)],"derivedFrom":[subQ1,subQ0]});Q91=makeQuery(id+"F4.imprint","IMPRINT",FACE,{"disambiguationData":[TD([[makeQuery(id+"F4.imprint","IMPRINT",EDGE,{"disambiguationData":[TD([[subQ2,-1.0]])],"derivedFrom":subQ0}),1.0]])]});}
            var Q92;
            {var subQ0=sQuery(id+"F4.wireOp",EDGE,"E5.6.4.0");var subQ1=makeQuery(id+"F1.opExtrude","CAP_EDGE",EDGE,{"disambiguationData":[OSD([sQuery(id+"F0.wireOp",EDGE,"E0.left")])],"isStart":false});var subQ2=makeQuery(id+"F4.imprint","INTERSECT",VERTEX,{"disambiguationData":[OD(0.0)],"derivedFrom":[subQ1,subQ0]});Q92=makeQuery(id+"F4.imprint","IMPRINT",FACE,{"disambiguationData":[TD([[makeQuery(id+"F4.imprint","IMPRINT",EDGE,{"disambiguationData":[TD([[subQ2,1.0]])],"derivedFrom":subQ0}),1.0]])]});}
            var Q93;
            {var subQ0=sQuery(id+"F4.wireOp",EDGE,"E5.6.5.0");var subQ1=makeQuery(id+"F1.opExtrude","CAP_EDGE",EDGE,{"disambiguationData":[OSD([sQuery(id+"F0.wireOp",EDGE,"E0.left")])],"isStart":false});var subQ2=makeQuery(id+"F4.imprint","INTERSECT",VERTEX,{"disambiguationData":[OD(0.0)],"derivedFrom":[subQ1,subQ0]});Q93=makeQuery(id+"F4.imprint","IMPRINT",FACE,{"disambiguationData":[TD([[makeQuery(id+"F4.imprint","IMPRINT",EDGE,{"disambiguationData":[TD([[subQ2,1.0]])],"derivedFrom":subQ0}),1.0]])]});}
            var Q94;
            {var subQ0=sQuery(id+"F4.wireOp",EDGE,"E5.6.6.0");var subQ1=makeQuery(id+"F1.opExtrude","CAP_EDGE",EDGE,{"disambiguationData":[OSD([sQuery(id+"F0.wireOp",EDGE,"E0.left")])],"isStart":false});var subQ2=makeQuery(id+"F4.imprint","INTERSECT",VERTEX,{"disambiguationData":[OD(0.0)],"derivedFrom":[subQ1,subQ0]});Q94=makeQuery(id+"F4.imprint","IMPRINT",FACE,{"disambiguationData":[TD([[makeQuery(id+"F4.imprint","IMPRINT",EDGE,{"disambiguationData":[TD([[subQ2,1.0]])],"derivedFrom":subQ0}),1.0]])]});}
            var Q95;
            {var subQ0=sQuery(id+"F4.wireOp",EDGE,"E5.6.7.0");var subQ1=makeQuery(id+"F1.opExtrude","CAP_EDGE",EDGE,{"disambiguationData":[OSD([sQuery(id+"F0.wireOp",EDGE,"E0.left")])],"isStart":false});var subQ2=makeQuery(id+"F4.imprint","INTERSECT",VERTEX,{"disambiguationData":[OD(0.0)],"derivedFrom":[subQ1,subQ0]});Q95=makeQuery(id+"F4.imprint","IMPRINT",FACE,{"disambiguationData":[TD([[makeQuery(id+"F4.imprint","IMPRINT",EDGE,{"disambiguationData":[TD([[subQ2,1.0]])],"derivedFrom":subQ0}),1.0]])]});}
            var Q96;
            {var subQ0=sQuery(id+"F4.wireOp",EDGE,"E6.0.7.0");var subQ1=makeQuery(id+"F1.opExtrude","CAP_EDGE",EDGE,{"disambiguationData":[OSD([sQuery(id+"F0.wireOp",EDGE,"E0.bottom")])],"isStart":false});var subQ2=makeQuery(id+"F4.imprint","INTERSECT",VERTEX,{"disambiguationData":[OD(0.0)],"derivedFrom":[subQ1,subQ0]});Q96=makeQuery(id+"F4.imprint","IMPRINT",FACE,{"disambiguationData":[TD([[makeQuery(id+"F4.imprint","IMPRINT",EDGE,{"disambiguationData":[TD([[subQ2,1.0]])],"derivedFrom":subQ0}),1.0]])]});}
            var Q97;
            {var subQ0=sQuery(id+"F4.wireOp",EDGE,"E6.1.7.0");var subQ1=makeQuery(id+"F1.opExtrude","CAP_EDGE",EDGE,{"disambiguationData":[OSD([sQuery(id+"F0.wireOp",EDGE,"E0.bottom")])],"isStart":false});var subQ2=makeQuery(id+"F4.imprint","INTERSECT",VERTEX,{"disambiguationData":[OD(0.0)],"derivedFrom":[subQ1,subQ0]});Q97=makeQuery(id+"F4.imprint","IMPRINT",FACE,{"disambiguationData":[TD([[makeQuery(id+"F4.imprint","IMPRINT",EDGE,{"disambiguationData":[TD([[subQ2,1.0]])],"derivedFrom":subQ0}),1.0]])]});}
            var Q98;
            {var subQ0=sQuery(id+"F4.wireOp",EDGE,"E6.2.7.0");var subQ1=makeQuery(id+"F1.opExtrude","CAP_EDGE",EDGE,{"disambiguationData":[OSD([sQuery(id+"F0.wireOp",EDGE,"E0.bottom")])],"isStart":false});var subQ2=makeQuery(id+"F4.imprint","INTERSECT",VERTEX,{"disambiguationData":[OD(0.0)],"derivedFrom":[subQ1,subQ0]});Q98=makeQuery(id+"F4.imprint","IMPRINT",FACE,{"disambiguationData":[TD([[makeQuery(id+"F4.imprint","IMPRINT",EDGE,{"disambiguationData":[TD([[subQ2,1.0]])],"derivedFrom":subQ0}),1.0]])]});}
            var Q99;
            {var subQ0=sQuery(id+"F4.wireOp",EDGE,"E6.3.7.0");var subQ1=makeQuery(id+"F1.opExtrude","CAP_EDGE",EDGE,{"disambiguationData":[OSD([sQuery(id+"F0.wireOp",EDGE,"E0.bottom")])],"isStart":false});var subQ2=makeQuery(id+"F4.imprint","INTERSECT",VERTEX,{"disambiguationData":[OD(0.0)],"derivedFrom":[subQ1,subQ0]});Q99=makeQuery(id+"F4.imprint","IMPRINT",FACE,{"disambiguationData":[TD([[makeQuery(id+"F4.imprint","IMPRINT",EDGE,{"disambiguationData":[TD([[subQ2,-1.0]])],"derivedFrom":subQ0}),1.0]])]});}
            var Q100;
            {var subQ0=sQuery(id+"F4.wireOp",EDGE,"E6.4.7.0");var subQ1=makeQuery(id+"F1.opExtrude","CAP_EDGE",EDGE,{"disambiguationData":[OSD([sQuery(id+"F0.wireOp",EDGE,"E0.bottom")])],"isStart":false});var subQ2=makeQuery(id+"F4.imprint","INTERSECT",VERTEX,{"disambiguationData":[OD(0.0)],"derivedFrom":[subQ1,subQ0]});Q100=makeQuery(id+"F4.imprint","IMPRINT",FACE,{"disambiguationData":[TD([[makeQuery(id+"F4.imprint","IMPRINT",EDGE,{"disambiguationData":[TD([[subQ2,-1.0]])],"derivedFrom":subQ0}),1.0]])]});}
            var Q101;
            {var subQ0=sQuery(id+"F4.wireOp",EDGE,"E6.5.7.0");var subQ1=makeQuery(id+"F1.opExtrude","CAP_EDGE",EDGE,{"disambiguationData":[OSD([sQuery(id+"F0.wireOp",EDGE,"E0.bottom")])],"isStart":false});var subQ2=makeQuery(id+"F4.imprint","INTERSECT",VERTEX,{"disambiguationData":[OD(0.0)],"derivedFrom":[subQ1,subQ0]});Q101=makeQuery(id+"F4.imprint","IMPRINT",FACE,{"disambiguationData":[TD([[makeQuery(id+"F4.imprint","IMPRINT",EDGE,{"disambiguationData":[TD([[subQ2,-1.0]])],"derivedFrom":subQ0}),1.0]])]});}
            var Q102;
            {var subQ0=sQuery(id+"F4.wireOp",EDGE,"E3");var subQ1=makeQuery(id+"F1.opExtrude","CAP_EDGE",EDGE,{"disambiguationData":[OSD([sQuery(id+"F0.wireOp",EDGE,"E0.top")])],"isStart":false});var subQ2=makeQuery(id+"F4.imprint","INTERSECT",VERTEX,{"derivedFrom":[subQ1,subQ0]});Q102=makeQuery(id+"F4.imprint","IMPRINT",FACE,{"disambiguationData":[TD([[makeQuery(id+"F4.imprint","IMPRINT",EDGE,{"disambiguationData":[TD([[subQ2,1.0]])],"derivedFrom":subQ0}),1.0]])]});}
            var Q103;
            {var subQ0=sQuery(id+"F4.wireOp",EDGE,"E5.6.0.0");var subQ1=makeQuery(id+"F1.opExtrude","CAP_EDGE",EDGE,{"disambiguationData":[OSD([sQuery(id+"F0.wireOp",EDGE,"E0.top")])],"isStart":false});var subQ2=makeQuery(id+"F4.imprint","INTERSECT",VERTEX,{"derivedFrom":[subQ1,subQ0]});Q103=makeQuery(id+"F4.imprint","IMPRINT",FACE,{"disambiguationData":[TD([[makeQuery(id+"F4.imprint","IMPRINT",EDGE,{"disambiguationData":[TD([[subQ2,-1.0]])],"derivedFrom":subQ0}),1.0]])]});}
            extrude(context, id + "F5", {"entities" : qUnion([Q0, Q1, Q2, Q3, Q4, Q5, Q6, Q7, Q8, Q9, Q10, Q11, Q12, Q13, Q14, Q15, Q16, Q17, Q18, Q19, Q20, Q21, Q22, Q23, Q24, Q25, Q26, Q27, Q28, Q29, Q30, Q31, Q32, Q33, Q34, Q35, Q36, Q37, Q38, Q39, Q40, Q41, Q42, Q43, Q44, Q45, Q46, Q47, Q48, Q49, Q50, Q51, Q52, Q53, Q54, Q55, Q56, Q57, Q58, Q59, Q60, Q61, Q62, Q63, Q64, Q65, Q66, Q67, Q68, Q69, Q70, Q71, Q72, Q73, Q74, Q75, Q76, Q77, Q78, Q79, Q80, Q81, Q82, Q83, Q84, Q85, Q86, Q87, Q88, Q89, Q90, Q91, Q92, Q93, Q94, Q95, Q96, Q97, Q98, Q99, Q100, Q101, Q102, Q103]), "operationType" : NewBodyOperationType.ADD, "depth" : 10 * mm, "offsetDistance" : 25 * mm});
        }
    });
